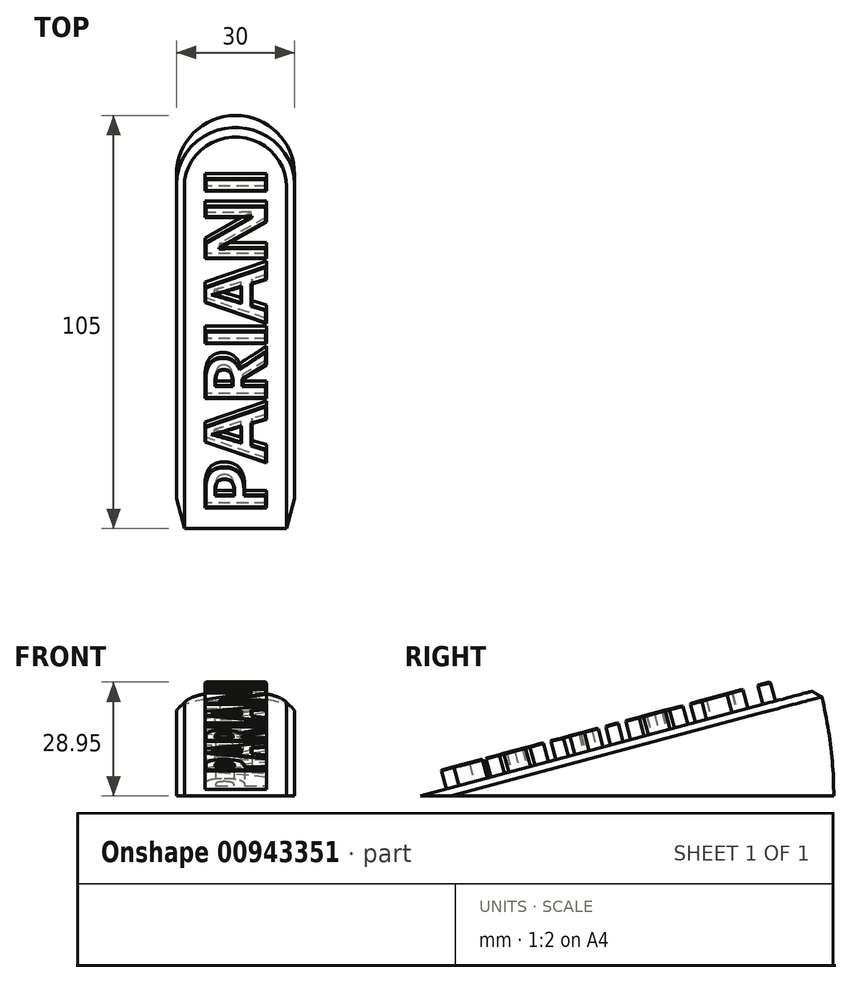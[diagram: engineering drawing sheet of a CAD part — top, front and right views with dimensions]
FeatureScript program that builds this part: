
annotation { "Feature Type Name" : "Feature", "Feature Type Description" : "" }
export const myFeature = defineFeature(function(context is Context, id is Id, definition is map)
    precondition{}
    {
        {
            var Q0;
            Q0=qCreatedBy(makeId("Top.planeOp"),FACE);
            var sketch = newSketch(context, id + "F0", { "sketchPlane" : qUnion([Q0])});
            skLineSegment(sketch, "E0.bottom", {"start": v(15, -60.54) * mm, "end": v(-15, -60.54) * mm});
            skLineSegment(sketch, "E0.left", {"start": v(15, -60.54) * mm, "end": v(15, 29.46) * mm});
            skLineSegment(sketch, "E0.right", {"start": v(-15, -60.54) * mm, "end": v(-15, 29.46) * mm});
            skPoint(sketch, "E0.middle", {"position": v(0, -15.54) * mm});
            skArc(sketch, "E1", {"start": v(-15, 29.46) * mm, "mid": v(0, 44.46) * mm, "end": v(15, 29.46) * mm});
            skSolve(sketch);
        }
        {
            var Q0;
            Q0 = qSketchRegion(id + "F0", true);
            var Q1;
            Q1=sQuery(id+"F0.wireOp",EDGE,"E0.bottom");
            revolve(context, id + "F1", {"surfaceOperationType" : NewSurfaceOperationType.NEW, "entities" : qUnion([Q0]), "axis" : qUnion([Q1]), "revolveType" : RevolveType.ONE_DIRECTION, "oppositeDirection" : true, "angle" : 15 * degree});
        }
        {
            var Q0;
            Q0=makeQuery(id+"F1.opRevolve","CAP_EDGE",EDGE,{"disambiguationData":[OSD([sQuery(id+"F0.wireOp",EDGE,"E0.right")])],"isStart":false});
            chamfer(context, id + "F2", {"entities" : qUnion([Q0]), "width" : 2 * mm, "tangentPropagation" : true});
        }
        {
            var Q0;
            Q0=makeQuery(id+"F1.opRevolve","CAP_FACE",FACE,{"disambiguationData":[OSD([sQuery(id+"F0.wireOp",EDGE,"E0.bottom"),sQuery(id+"F0.wireOp",EDGE,"E0.left"),sQuery(id+"F0.wireOp",EDGE,"E0.right"),sQuery(id+"F0.wireOp",EDGE,"E1")])],"isStart":false});
            var sketch = newSketch(context, id + "F3", { "sketchPlane" : qUnion([Q0])});
            skText(sketch, "E2", { "text": "PARIANI", "fontName": "OpenSans-Bold.ttf"});
            const initialGuessF3  = {"E2": [0.00787, -0.05365, 0, 1, 0.01573]};
            skSetInitialGuess(sketch, initialGuessF3);
            skSolve(sketch);
        }
        {
            var Q0;
            Q0 = qSketchRegion(id + "F3", true);
            extrude(context, id + "F4", {"entities" : qUnion([Q0]), "operationType" : NewBodyOperationType.ADD, "depth" : 5 * mm, "offsetDistance" : 25 * mm});
        }
        {
            var Q0;
            Q0=makeQuery(id+"F4.opExtrude","CAP_FACE",FACE,{"disambiguationData":[OSD([sQuery(id+"F3.wireOp",EDGE,"E2.sketch_text.stroke-0"),sQuery(id+"F3.wireOp",EDGE,"E2.sketch_text.stroke-1"),sQuery(id+"F3.wireOp",EDGE,"E2.sketch_text.stroke-2"),sQuery(id+"F3.wireOp",EDGE,"E2.sketch_text.stroke-3"),sQuery(id+"F3.wireOp",EDGE,"E2.sketch_text.stroke-4"),sQuery(id+"F3.wireOp",EDGE,"E2.sketch_text.stroke-5"),sQuery(id+"F3.wireOp",EDGE,"E2.sketch_text.stroke-6"),sQuery(id+"F3.wireOp",EDGE,"E2.sketch_text.stroke-7"),sQuery(id+"F3.wireOp",EDGE,"E2.sketch_text.stroke-8"),sQuery(id+"F3.wireOp",EDGE,"E2.sketch_text.stroke-9"),sQuery(id+"F3.wireOp",EDGE,"E2.sketch_text.stroke-10"),sQuery(id+"F3.wireOp",EDGE,"E2.sketch_text.stroke-11"),sQuery(id+"F3.wireOp",EDGE,"E2.sketch_text.stroke-12"),sQuery(id+"F3.wireOp",EDGE,"E2.sketch_text.stroke-13"),sQuery(id+"F3.wireOp",EDGE,"E2.sketch_text.stroke-14"),sQuery(id+"F3.wireOp",EDGE,"E2.sketch_text.stroke-15")])],"isStart":false});
            var Q1;
            Q1=makeQuery(id+"F4.opExtrude","CAP_FACE",FACE,{"disambiguationData":[OSD([sQuery(id+"F3.wireOp",EDGE,"E2.sketch_text.stroke-16"),sQuery(id+"F3.wireOp",EDGE,"E2.sketch_text.stroke-17"),sQuery(id+"F3.wireOp",EDGE,"E2.sketch_text.stroke-18"),sQuery(id+"F3.wireOp",EDGE,"E2.sketch_text.stroke-19"),sQuery(id+"F3.wireOp",EDGE,"E2.sketch_text.stroke-20"),sQuery(id+"F3.wireOp",EDGE,"E2.sketch_text.stroke-21"),sQuery(id+"F3.wireOp",EDGE,"E2.sketch_text.stroke-22"),sQuery(id+"F3.wireOp",EDGE,"E2.sketch_text.stroke-23"),sQuery(id+"F3.wireOp",EDGE,"E2.sketch_text.stroke-24"),sQuery(id+"F3.wireOp",EDGE,"E2.sketch_text.stroke-25"),sQuery(id+"F3.wireOp",EDGE,"E2.sketch_text.stroke-26"),sQuery(id+"F3.wireOp",EDGE,"E2.sketch_text.stroke-27")])],"isStart":false});
            var Q2;
            Q2=makeQuery(id+"F4.opExtrude","CAP_FACE",FACE,{"disambiguationData":[OSD([sQuery(id+"F3.wireOp",EDGE,"E2.sketch_text.stroke-28"),sQuery(id+"F3.wireOp",EDGE,"E2.sketch_text.stroke-29"),sQuery(id+"F3.wireOp",EDGE,"E2.sketch_text.stroke-30"),sQuery(id+"F3.wireOp",EDGE,"E2.sketch_text.stroke-31"),sQuery(id+"F3.wireOp",EDGE,"E2.sketch_text.stroke-32"),sQuery(id+"F3.wireOp",EDGE,"E2.sketch_text.stroke-33"),sQuery(id+"F3.wireOp",EDGE,"E2.sketch_text.stroke-34"),sQuery(id+"F3.wireOp",EDGE,"E2.sketch_text.stroke-35"),sQuery(id+"F3.wireOp",EDGE,"E2.sketch_text.stroke-36"),sQuery(id+"F3.wireOp",EDGE,"E2.sketch_text.stroke-37"),sQuery(id+"F3.wireOp",EDGE,"E2.sketch_text.stroke-38"),sQuery(id+"F3.wireOp",EDGE,"E2.sketch_text.stroke-39"),sQuery(id+"F3.wireOp",EDGE,"E2.sketch_text.stroke-40"),sQuery(id+"F3.wireOp",EDGE,"E2.sketch_text.stroke-41"),sQuery(id+"F3.wireOp",EDGE,"E2.sketch_text.stroke-42"),sQuery(id+"F3.wireOp",EDGE,"E2.sketch_text.stroke-43"),sQuery(id+"F3.wireOp",EDGE,"E2.sketch_text.stroke-44"),sQuery(id+"F3.wireOp",EDGE,"E2.sketch_text.stroke-45"),sQuery(id+"F3.wireOp",EDGE,"E2.sketch_text.stroke-46")])],"isStart":false});
            var Q3;
            Q3=makeQuery(id+"F4.opExtrude","CAP_FACE",FACE,{"disambiguationData":[OSD([sQuery(id+"F3.wireOp",EDGE,"E2.sketch_text.stroke-47"),sQuery(id+"F3.wireOp",EDGE,"E2.sketch_text.stroke-48"),sQuery(id+"F3.wireOp",EDGE,"E2.sketch_text.stroke-49"),sQuery(id+"F3.wireOp",EDGE,"E2.sketch_text.stroke-50")])],"isStart":false});
            var Q4;
            Q4=makeQuery(id+"F4.opExtrude","CAP_FACE",FACE,{"disambiguationData":[OSD([sQuery(id+"F3.wireOp",EDGE,"E2.sketch_text.stroke-51"),sQuery(id+"F3.wireOp",EDGE,"E2.sketch_text.stroke-52"),sQuery(id+"F3.wireOp",EDGE,"E2.sketch_text.stroke-53"),sQuery(id+"F3.wireOp",EDGE,"E2.sketch_text.stroke-54"),sQuery(id+"F3.wireOp",EDGE,"E2.sketch_text.stroke-55"),sQuery(id+"F3.wireOp",EDGE,"E2.sketch_text.stroke-56"),sQuery(id+"F3.wireOp",EDGE,"E2.sketch_text.stroke-57"),sQuery(id+"F3.wireOp",EDGE,"E2.sketch_text.stroke-58"),sQuery(id+"F3.wireOp",EDGE,"E2.sketch_text.stroke-59"),sQuery(id+"F3.wireOp",EDGE,"E2.sketch_text.stroke-60"),sQuery(id+"F3.wireOp",EDGE,"E2.sketch_text.stroke-61"),sQuery(id+"F3.wireOp",EDGE,"E2.sketch_text.stroke-62")])],"isStart":false});
            var Q5;
            Q5=makeQuery(id+"F4.opExtrude","CAP_FACE",FACE,{"disambiguationData":[OSD([sQuery(id+"F3.wireOp",EDGE,"E2.sketch_text.stroke-63"),sQuery(id+"F3.wireOp",EDGE,"E2.sketch_text.stroke-64"),sQuery(id+"F3.wireOp",EDGE,"E2.sketch_text.stroke-65"),sQuery(id+"F3.wireOp",EDGE,"E2.sketch_text.stroke-66"),sQuery(id+"F3.wireOp",EDGE,"E2.sketch_text.stroke-67"),sQuery(id+"F3.wireOp",EDGE,"E2.sketch_text.stroke-68"),sQuery(id+"F3.wireOp",EDGE,"E2.sketch_text.stroke-69"),sQuery(id+"F3.wireOp",EDGE,"E2.sketch_text.stroke-70"),sQuery(id+"F3.wireOp",EDGE,"E2.sketch_text.stroke-71"),sQuery(id+"F3.wireOp",EDGE,"E2.sketch_text.stroke-72"),sQuery(id+"F3.wireOp",EDGE,"E2.sketch_text.stroke-73"),sQuery(id+"F3.wireOp",EDGE,"E2.sketch_text.stroke-74"),sQuery(id+"F3.wireOp",EDGE,"E2.sketch_text.stroke-75"),sQuery(id+"F3.wireOp",EDGE,"E2.sketch_text.stroke-76")])],"isStart":false});
            var Q6;
            Q6=makeQuery(id+"F4.opExtrude","CAP_FACE",FACE,{"disambiguationData":[OSD([sQuery(id+"F3.wireOp",EDGE,"E2.sketch_text.stroke-77"),sQuery(id+"F3.wireOp",EDGE,"E2.sketch_text.stroke-78"),sQuery(id+"F3.wireOp",EDGE,"E2.sketch_text.stroke-79"),sQuery(id+"F3.wireOp",EDGE,"E2.sketch_text.stroke-80")])],"isStart":false});
            chamfer(context, id + "F5", {"entities" : qUnion([Q0, Q1, Q2, Q3, Q4, Q5, Q6]), "width" : 0.2 * mm, "tangentPropagation" : true});
        }
    });
